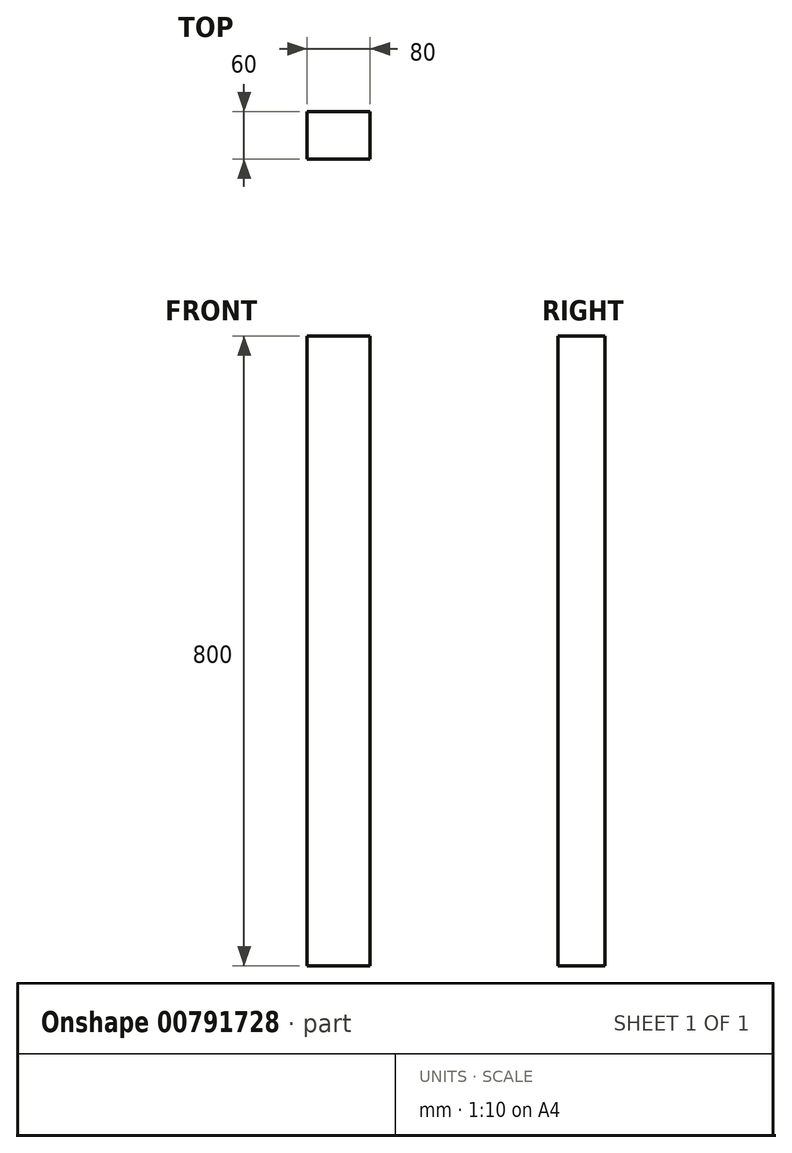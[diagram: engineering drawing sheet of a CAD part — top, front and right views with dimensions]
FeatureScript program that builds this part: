
annotation { "Feature Type Name" : "Feature", "Feature Type Description" : "" }
export const myFeature = defineFeature(function(context is Context, id is Id, definition is map)
    precondition{}
    {
        {
            var Q0;
            Q0=qCreatedBy(makeId("Top.planeOp"),FACE);
            var sketch = newSketch(context, id + "F0", { "sketchPlane" : qUnion([Q0])});
            skLineSegment(sketch, "E0.bottom", {"start": v(-18.48, 46.6) * mm, "end": v(61.52, 46.6) * mm});
            skLineSegment(sketch, "E0.top", {"start": v(-18.48, -13.4) * mm, "end": v(61.52, -13.4) * mm});
            skLineSegment(sketch, "E0.left", {"start": v(-18.48, 46.6) * mm, "end": v(-18.48, -13.4) * mm});
            skLineSegment(sketch, "E0.right", {"start": v(61.52, 46.6) * mm, "end": v(61.52, -13.4) * mm});
            skSolve(sketch);
        }
        {
            var Q0;
            Q0=makeQuery(id+"F0.imprint","IMPRINT",FACE,{"disambiguationData":[TD([[makeQuery(id+"F0.imprint","IMPRINT",EDGE,{"derivedFrom":sQuery(id+"F0.wireOp",EDGE,"E0.bottom")}),-1.0]])]});
            extrude(context, id + "F1", {"entities" : qUnion([Q0]), "depth" : 800 * mm, "offsetDistance" : 25 * mm});
        }
    });
